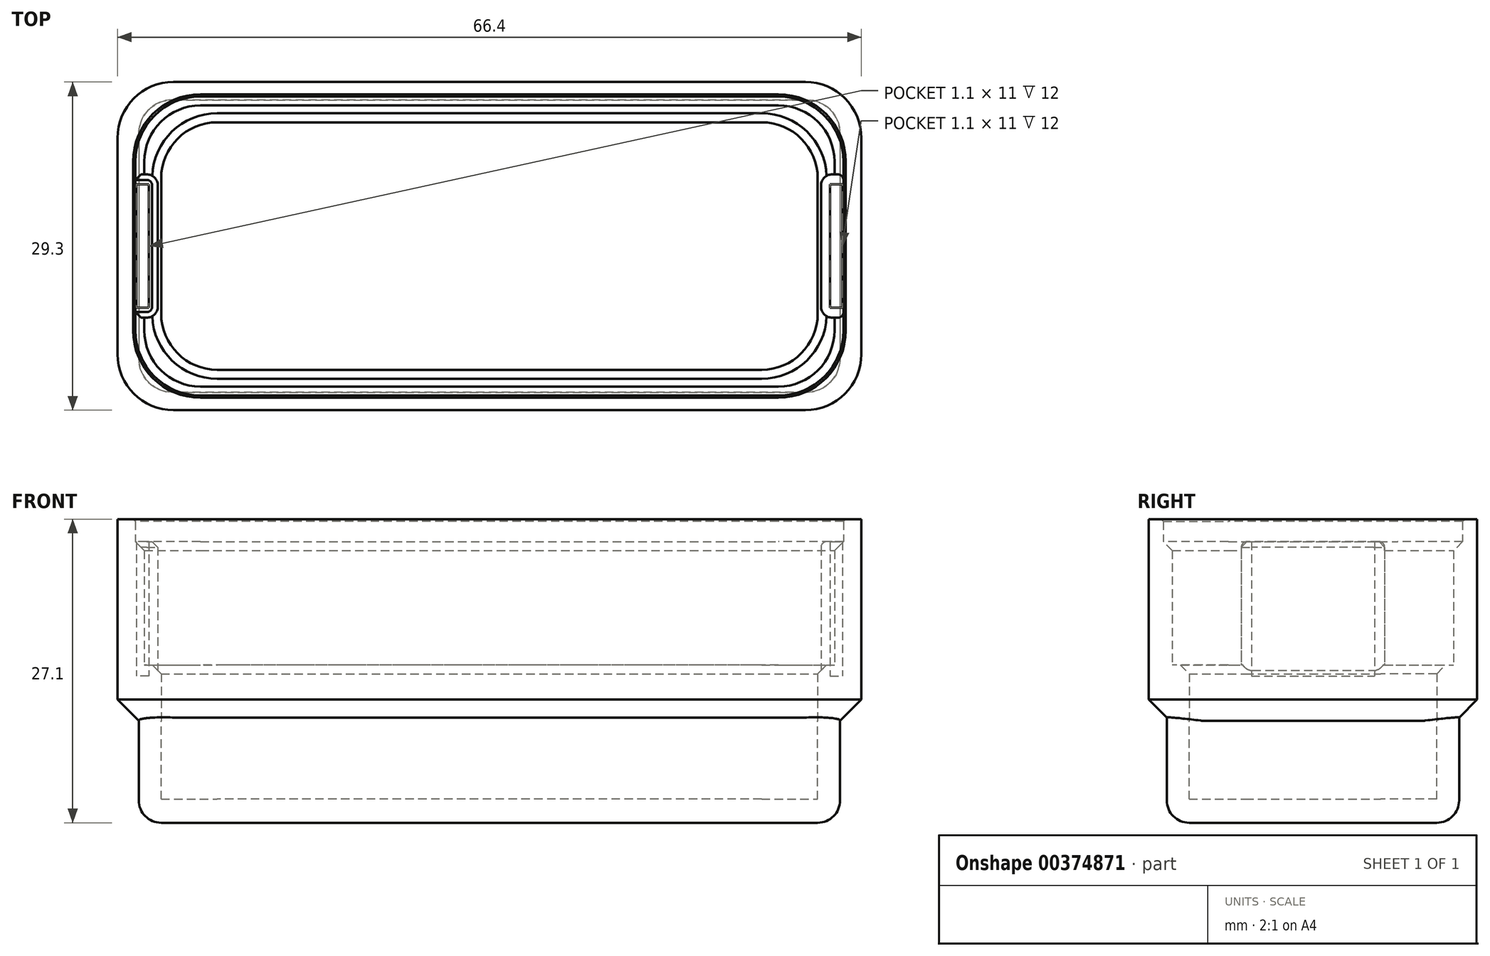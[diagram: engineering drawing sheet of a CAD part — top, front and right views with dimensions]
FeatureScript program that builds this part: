
annotation { "Feature Type Name" : "Feature", "Feature Type Description" : "" }
export const myFeature = defineFeature(function(context is Context, id is Id, definition is map)
    precondition{}
    {
        {
            var Q0;
            Q0=qCreatedBy(makeId("Top.planeOp"),FACE);
            var sketch = newSketch(context, id + "F0", { "sketchPlane" : qUnion([Q0])});
            skLineSegment(sketch, "E0.bottom", {"start": v(30.5, -12.25) * mm, "end": v(-30.5, -12.25) * mm, "construction": true});
            skLineSegment(sketch, "E0.top", {"start": v(30.5, 12.25) * mm, "end": v(-30.5, 12.25) * mm, "construction": true});
            skLineSegment(sketch, "E0.left", {"start": v(30.5, -12.25) * mm, "end": v(30.5, 12.25) * mm, "construction": true});
            skLineSegment(sketch, "E0.right", {"start": v(-30.5, -12.25) * mm, "end": v(-30.5, 12.25) * mm, "construction": true});
            skPoint(sketch, "E0.middle", {"position": v(0, 0) * mm});
            skLineSegment(sketch, "E1.bottom", {"start": v(30.8, -12.55) * mm, "end": v(-30.8, -12.55) * mm});
            skLineSegment(sketch, "E1.top", {"start": v(30.8, 12.55) * mm, "end": v(-30.8, 12.55) * mm});
            skLineSegment(sketch, "E1.left", {"start": v(30.8, -12.55) * mm, "end": v(30.8, 12.55) * mm});
            skLineSegment(sketch, "E1.right", {"start": v(-30.8, -12.55) * mm, "end": v(-30.8, -6.4) * mm});
            skLineSegment(sketch, "E2.bottom", {"start": v(33.2, -14.65) * mm, "end": v(-33.2, -14.65) * mm});
            skLineSegment(sketch, "E2.top", {"start": v(33.2, 14.65) * mm, "end": v(-33.2, 14.65) * mm});
            skLineSegment(sketch, "E2.left", {"start": v(33.2, -14.65) * mm, "end": v(33.2, 14.65) * mm});
            skLineSegment(sketch, "E2.right", {"start": v(-33.2, -14.65) * mm, "end": v(-33.2, 14.65) * mm});
            skPoint(sketch, "E3.middle", {"position": v(0, 14.35) * mm});
            skPoint(sketch, "E4.middle", {"position": v(0, -14.35) * mm});
            skPoint(sketch, "E4.middle.positionSnap0", {"position": v(0, -12.25) * mm});
            skPoint(sketch, "E4.centerSnap0", {"position": v(0, -12.25) * mm});
            skLineSegment(sketch, "E5.bottom", {"start": v(-29.6, -6.4) * mm, "end": v(-30.8, -6.4) * mm});
            skLineSegment(sketch, "E5.top", {"start": v(-29.6, 6.4) * mm, "end": v(-30.8, 6.4) * mm});
            skLineSegment(sketch, "E5.left", {"start": v(-29.6, -6.4) * mm, "end": v(-29.6, 6.4) * mm});
            skLineSegment(sketch, "E6.trimOffspring", {"start": v(-30.8, 6.4) * mm, "end": v(-30.8, 12.55) * mm});
            skLineSegment(sketch, "E7.bottom", {"start": v(-30.4, -5.5) * mm, "end": v(-31.5, -5.5) * mm});
            skLineSegment(sketch, "E7.top", {"start": v(-30.4, 5.5) * mm, "end": v(-31.5, 5.5) * mm});
            skLineSegment(sketch, "E7.left", {"start": v(-30.4, -5.5) * mm, "end": v(-30.4, 5.5) * mm});
            skLineSegment(sketch, "E7.right", {"start": v(-31.5, -5.5) * mm, "end": v(-31.5, 5.5) * mm});
            skPoint(sketch, "E8", {"position": v(-29.6, 0) * mm});
            skPoint(sketch, "E9", {"position": v(-30.4, 0) * mm});
            skLineSegment(sketch, "E10", {"start": v(0, 20.82) * mm, "end": v(0, -18.98) * mm, "construction": true});
            skLineSegment(sketch, "E11.MirrorCS", {"start": v(30.4, 5.5) * mm, "end": v(31.5, 5.5) * mm});
            skLineSegment(sketch, "E12.MirrorCS", {"start": v(30.4, -5.5) * mm, "end": v(30.4, 5.5) * mm});
            skLineSegment(sketch, "E13.MirrorCS", {"start": v(31.5, -5.5) * mm, "end": v(31.5, 5.5) * mm});
            skLineSegment(sketch, "E14.MirrorCS", {"start": v(30.4, -5.5) * mm, "end": v(31.5, -5.5) * mm});
            skLineSegment(sketch, "E15.MirrorCS", {"start": v(29.6, -6.4) * mm, "end": v(29.6, 6.4) * mm});
            skLineSegment(sketch, "E16.MirrorCS", {"start": v(29.6, -6.4) * mm, "end": v(30.8, -6.4) * mm});
            skLineSegment(sketch, "E17.MirrorCS", {"start": v(29.6, 6.4) * mm, "end": v(30.8, 6.4) * mm});
            skSolve(sketch);
        }
        {
            var Q0;
            Q0=makeQuery(id+"F0.imprint","IMPRINT",FACE,{"disambiguationData":[TD([[makeQuery(id+"F0.imprint","IMPRINT",EDGE,{"derivedFrom":sQuery(id+"F0.wireOp",EDGE,"E4.bottom")}),-1.0]])]});
            var Q1;
            Q1=makeQuery(id+"F0.imprint","IMPRINT",FACE,{"disambiguationData":[TD([[makeQuery(id+"F0.imprint","IMPRINT",EDGE,{"derivedFrom":sQuery(id+"F0.wireOp",EDGE,"E3.bottom")}),-1.0]])]});
            var Q2;
            {var subQ0=sQuery(id+"F0.wireOp",EDGE,"E12.MirrorCS");Q2=makeQuery(id+"F0.imprint","IMPRINT",FACE,{"disambiguationData":[TD([[makeQuery(id+"F0.imprint","IMPRINT",EDGE,{"derivedFrom":subQ0}),1.0]])]});}
            var Q3;
            Q3=makeQuery(id+"F0.imprint","IMPRINT",FACE,{"disambiguationData":[TD([[makeQuery(id+"F0.imprint","IMPRINT",EDGE,{"derivedFrom":sQuery(id+"F0.wireOp",EDGE,"E7.bottom")}),-1.0]])]});
            var Q4;
            {var subQ5=sQuery(id+"F0.wireOp",EDGE,"E1.bottom");Q4=makeQuery(id+"F0.imprint","IMPRINT",FACE,{"disambiguationData":[TD([[makeQuery(id+"F0.imprint","IMPRINT",EDGE,{"derivedFrom":subQ5}),1.0]])]});}
            var Q5;
            {var subQ5=sQuery(id+"F0.wireOp",EDGE,"E13.MirrorCS");Q5=makeQuery(id+"F0.imprint","IMPRINT",FACE,{"disambiguationData":[TD([[makeQuery(id+"F0.imprint","IMPRINT",EDGE,{"derivedFrom":subQ5}),1.0]])]});}
            var Q6;
            {var subQ0=sQuery(id+"F0.wireOp",EDGE,"E1.bottom");Q6=makeQuery(id+"F0.imprint","IMPRINT",FACE,{"disambiguationData":[TD([[makeQuery(id+"F0.imprint","IMPRINT",EDGE,{"derivedFrom":subQ0}),-1.0]])]});}
            var Q7;
            {var subQ5=sQuery(id+"F0.wireOp",EDGE,"E12.MirrorCS");Q7=makeQuery(id+"F0.imprint","IMPRINT",FACE,{"disambiguationData":[TD([[makeQuery(id+"F0.imprint","IMPRINT",EDGE,{"derivedFrom":subQ5}),-1.0]])]});}
            extrude(context, id + "F1", {"entities" : qUnion([Q0, Q1, Q2, Q3, Q4, Q5, Q6, Q7]), "oppositeDirection" : true, "depth" : 0.1 * mm});
        }
        {
            var Q0;
            Q0=makeQuery(id+"F0.imprint","IMPRINT",FACE,{"disambiguationData":[TD([[makeQuery(id+"F0.imprint","IMPRINT",EDGE,{"derivedFrom":sQuery(id+"F0.wireOp",EDGE,"E1.bottom")}),1.0]])]});
            var Q1;
            {var subQ0=sQuery(id+"F0.wireOp",EDGE,"E12.MirrorCS");Q1=makeQuery(id+"F0.imprint","IMPRINT",FACE,{"disambiguationData":[TD([[makeQuery(id+"F0.imprint","IMPRINT",EDGE,{"derivedFrom":subQ0}),1.0]])]});}
            extrude(context, id + "F2", {"entities" : qUnion([Q0, Q1]), "operationType" : NewBodyOperationType.ADD, "depth" : 16 * mm});
        }
        {
            var Q0;
            Q0=makeQuery(id+"F0.imprint","IMPRINT",FACE,{"disambiguationData":[TD([[makeQuery(id+"F0.imprint","IMPRINT",EDGE,{"derivedFrom":sQuery(id+"F0.wireOp",EDGE,"E1.bottom")}),-1.0]])]});
            var sketch = newSketch(context, id + "F3", { "sketchPlane" : qUnion([Q0])});
            skLineSegment(sketch, "E18.bottom", {"start": v(29.3, -11.05) * mm, "end": v(-29.3, -11.05) * mm});
            skLineSegment(sketch, "E18.top", {"start": v(29.3, 11.05) * mm, "end": v(-29.3, 11.05) * mm});
            skLineSegment(sketch, "E18.left", {"start": v(29.3, -11.05) * mm, "end": v(29.3, 11.05) * mm});
            skLineSegment(sketch, "E18.right", {"start": v(-29.3, -11.05) * mm, "end": v(-29.3, 11.05) * mm});
            skPoint(sketch, "E18.middle", {"position": v(0, 0) * mm});
            skSolve(sketch);
        }
        {
            var Q0;
            Q0 = qSketchRegion(id + "F3", true);
            extrude(context, id + "F4", {"entities" : qUnion([Q0]), "operationType" : NewBodyOperationType.REMOVE, "depth" : 25 * mm});
        }
        {
            var Q0;
            Q0=makeQuery(id+"F3.imprint","IMPRINT",FACE,{"disambiguationData":[TD([[makeQuery(id+"F3.imprint","IMPRINT",EDGE,{"derivedFrom":sQuery(id+"F3.wireOp",EDGE,"E18.bottom")}),1.0]])]});
            extrude(context, id + "F5", {"entities" : qUnion([Q0]), "operationType" : NewBodyOperationType.ADD, "depth" : 5 * mm});
        }
        {
            var Q0;
            Q0=makeQuery(id+"F0.imprint","IMPRINT",FACE,{"disambiguationData":[TD([[makeQuery(id+"F0.imprint","IMPRINT",EDGE,{"derivedFrom":sQuery(id+"F0.wireOp",EDGE,"E7.bottom")}),-1.0]])]});
            var Q1;
            {var subQ5=sQuery(id+"F0.wireOp",EDGE,"E12.MirrorCS");Q1=makeQuery(id+"F0.imprint","IMPRINT",FACE,{"disambiguationData":[TD([[makeQuery(id+"F0.imprint","IMPRINT",EDGE,{"derivedFrom":subQ5}),-1.0]])]});}
            var Q2;
            {var subQ5=sQuery(id+"F0.wireOp",EDGE,"E13.MirrorCS");Q2=makeQuery(id+"F0.imprint","IMPRINT",FACE,{"disambiguationData":[TD([[makeQuery(id+"F0.imprint","IMPRINT",EDGE,{"derivedFrom":subQ5}),1.0]])]});}
            extrude(context, id + "F6", {"entities" : qUnion([Q0, Q1, Q2]), "operationType" : NewBodyOperationType.ADD, "depth" : 4 * mm});
        }
        {
            var Q0;
            {var subQ0=sQuery(id+"F0.wireOp",EDGE,"E2.right");var subQ1=sQuery(id+"F0.wireOp",EDGE,"E2.bottom");Q0=makeQuery(id+"F2.boolean.opBoolean","MERGE",EDGE,{"derivedFrom":[makeQuery(id+"F1.opExtrude","SWEPT_EDGE",EDGE,{"disambiguationData":[OSD([subQ1,subQ0])]}),makeQuery(id+"F2.opExtrude","SWEPT_EDGE",EDGE,{"disambiguationData":[OSD([subQ1,subQ0])]})]});}
            var Q1;
            {var subQ0=sQuery(id+"F0.wireOp",EDGE,"E2.left");var subQ1=sQuery(id+"F0.wireOp",EDGE,"E2.bottom");Q1=makeQuery(id+"F2.boolean.opBoolean","MERGE",EDGE,{"derivedFrom":[makeQuery(id+"F1.opExtrude","SWEPT_EDGE",EDGE,{"disambiguationData":[OSD([subQ1,subQ0])]}),makeQuery(id+"F2.opExtrude","SWEPT_EDGE",EDGE,{"disambiguationData":[OSD([subQ1,subQ0])]})]});}
            var Q2;
            {var subQ0=sQuery(id+"F0.wireOp",EDGE,"E2.left");var subQ1=sQuery(id+"F0.wireOp",EDGE,"E2.top");Q2=makeQuery(id+"F2.boolean.opBoolean","MERGE",EDGE,{"derivedFrom":[makeQuery(id+"F1.opExtrude","SWEPT_EDGE",EDGE,{"disambiguationData":[OSD([subQ1,subQ0])]}),makeQuery(id+"F2.opExtrude","SWEPT_EDGE",EDGE,{"disambiguationData":[OSD([subQ1,subQ0])]})]});}
            var Q3;
            {var subQ0=sQuery(id+"F0.wireOp",EDGE,"E2.right");var subQ1=sQuery(id+"F0.wireOp",EDGE,"E2.top");Q3=makeQuery(id+"F2.boolean.opBoolean","MERGE",EDGE,{"derivedFrom":[makeQuery(id+"F1.opExtrude","SWEPT_EDGE",EDGE,{"disambiguationData":[OSD([subQ1,subQ0])]}),makeQuery(id+"F2.opExtrude","SWEPT_EDGE",EDGE,{"disambiguationData":[OSD([subQ1,subQ0])]})]});}
            var Q4;
            Q4=makeQuery(id+"F2.opExtrude","SWEPT_EDGE",EDGE,{"disambiguationData":[OSD([sQuery(id+"F0.wireOp",EDGE,"E1.top"),sQuery(id+"F0.wireOp",EDGE,"E6.trimOffspring")])]});
            var Q5;
            Q5=makeQuery(id+"F2.opExtrude","SWEPT_EDGE",EDGE,{"disambiguationData":[OSD([sQuery(id+"F0.wireOp",EDGE,"E1.top"),sQuery(id+"F0.wireOp",EDGE,"E1.left")])]});
            var Q6;
            Q6=makeQuery(id+"F2.opExtrude","SWEPT_EDGE",EDGE,{"disambiguationData":[OSD([sQuery(id+"F0.wireOp",EDGE,"E1.bottom"),sQuery(id+"F0.wireOp",EDGE,"E1.right")])]});
            var Q7;
            Q7=makeQuery(id+"F2.opExtrude","SWEPT_EDGE",EDGE,{"disambiguationData":[OSD([sQuery(id+"F0.wireOp",EDGE,"E1.bottom"),sQuery(id+"F0.wireOp",EDGE,"E1.left")])]});
            fillet(context, id + "F7", {"entities" : qUnion([Q0, Q1, Q2, Q3, Q4, Q5, Q6, Q7]), "radius" : 5 * mm, "tangentPropagation" : true, "allowEdgeOverflow" : false});
        }
        {
            var Q0;
            Q0=makeQuery(id+"F2.opExtrude","SWEPT_EDGE",EDGE,{"disambiguationData":[OSD([sQuery(id+"F0.wireOp",EDGE,"E5.top"),sQuery(id+"F0.wireOp",EDGE,"E5.left")])]});
            var Q1;
            Q1=makeQuery(id+"F2.opExtrude","SWEPT_EDGE",EDGE,{"disambiguationData":[OSD([sQuery(id+"F0.wireOp",EDGE,"E5.bottom"),sQuery(id+"F0.wireOp",EDGE,"E5.left")])]});
            var Q2;
            Q2=makeQuery(id+"F2.opExtrude","SWEPT_EDGE",EDGE,{"disambiguationData":[OSD([sQuery(id+"F0.wireOp",EDGE,"E15.MirrorCS"),sQuery(id+"F0.wireOp",EDGE,"E17.MirrorCS")])]});
            var Q3;
            Q3=makeQuery(id+"F2.opExtrude","SWEPT_EDGE",EDGE,{"disambiguationData":[OSD([sQuery(id+"F0.wireOp",EDGE,"E15.MirrorCS"),sQuery(id+"F0.wireOp",EDGE,"E16.MirrorCS")])]});
            fillet(context, id + "F8", {"entities" : qUnion([Q0, Q1, Q2, Q3]), "radius" : 1 * mm, "tangentPropagation" : true, "allowEdgeOverflow" : false});
        }
        {
            var Q0;
            Q0=makeQuery(id+"F5.opExtrude","SWEPT_EDGE",EDGE,{"disambiguationData":[OSD([sQuery(id+"F3.wireOp",EDGE,"E18.top"),sQuery(id+"F3.wireOp",EDGE,"E18.left")])]});
            var Q1;
            Q1=makeQuery(id+"F5.opExtrude","SWEPT_EDGE",EDGE,{"disambiguationData":[OSD([sQuery(id+"F3.wireOp",EDGE,"E18.top"),sQuery(id+"F3.wireOp",EDGE,"E18.right")])]});
            var Q2;
            Q2=makeQuery(id+"F5.opExtrude","SWEPT_EDGE",EDGE,{"disambiguationData":[OSD([sQuery(id+"F3.wireOp",EDGE,"E18.bottom"),sQuery(id+"F3.wireOp",EDGE,"E18.right")])]});
            var Q3;
            Q3=makeQuery(id+"F5.opExtrude","SWEPT_EDGE",EDGE,{"disambiguationData":[OSD([sQuery(id+"F3.wireOp",EDGE,"E18.bottom"),sQuery(id+"F3.wireOp",EDGE,"E18.left")])]});
            fillet(context, id + "F9", {"entities" : qUnion([Q0, Q1, Q2, Q3]), "radius" : 5 * mm, "tangentPropagation" : true, "allowEdgeOverflow" : false});
        }
        {
            var Q0;
            Q0=makeQuery(id+"F1.opExtrude","CAP_FACE",FACE,{"disambiguationData":[OSD([sQuery(id+"F0.wireOp",EDGE,"E2.bottom"),sQuery(id+"F0.wireOp",EDGE,"E2.top"),sQuery(id+"F0.wireOp",EDGE,"E2.left"),sQuery(id+"F0.wireOp",EDGE,"E2.right")])],"isStart":false});
            var sketch = newSketch(context, id + "F10", { "sketchPlane" : qUnion([Q0])});
            skLineSegment(sketch, "E19.bottom", {"start": v(31.3, -13.05) * mm, "end": v(-31.3, -13.05) * mm});
            skLineSegment(sketch, "E19.top", {"start": v(31.3, 13.05) * mm, "end": v(-31.3, 13.05) * mm});
            skLineSegment(sketch, "E19.left", {"start": v(31.3, -13.05) * mm, "end": v(31.3, 13.05) * mm});
            skLineSegment(sketch, "E19.right", {"start": v(-31.3, -13.05) * mm, "end": v(-31.3, 13.05) * mm});
            skPoint(sketch, "E19.middle", {"position": v(0, 0) * mm});
            skSolve(sketch);
        }
        {
            var Q0;
            Q0=makeQuery(id+"F10.imprint","IMPRINT",FACE,{"disambiguationData":[TD([[makeQuery(id+"F10.imprint","IMPRINT",EDGE,{"derivedFrom":sQuery(id+"F10.wireOp",EDGE,"E19.bottom")}),-1.0]])]});
            extrude(context, id + "F11", {"entities" : qUnion([Q0]), "operationType" : NewBodyOperationType.ADD, "depth" : 9 * mm});
        }
        {
            var Q0;
            Q0=makeQuery(id+"F3.imprint","IMPRINT",FACE,{"disambiguationData":[TD([[makeQuery(id+"F3.imprint","IMPRINT",EDGE,{"derivedFrom":sQuery(id+"F3.wireOp",EDGE,"E18.bottom")}),-1.0]])]});
            extrude(context, id + "F12", {"entities" : qUnion([Q0]), "operationType" : NewBodyOperationType.REMOVE, "oppositeDirection" : true, "depth" : 7 * mm});
        }
        {
            var Q0;
            Q0=makeQuery(id+"F12.boolean.opBoolean","COPY",EDGE,{"derivedFrom":makeQuery(id+"F12.opExtrude","SWEPT_EDGE",EDGE,{"disambiguationData":[OSD([sQuery(id+"F3.wireOp",EDGE,"E18.top"),sQuery(id+"F3.wireOp",EDGE,"E18.right")])]})});
            var Q1;
            Q1=makeQuery(id+"F12.boolean.opBoolean","COPY",EDGE,{"derivedFrom":makeQuery(id+"F12.opExtrude","SWEPT_EDGE",EDGE,{"disambiguationData":[OSD([sQuery(id+"F3.wireOp",EDGE,"E18.top"),sQuery(id+"F3.wireOp",EDGE,"E18.left")])]})});
            var Q2;
            Q2=makeQuery(id+"F12.boolean.opBoolean","COPY",EDGE,{"derivedFrom":makeQuery(id+"F12.opExtrude","SWEPT_EDGE",EDGE,{"disambiguationData":[OSD([sQuery(id+"F3.wireOp",EDGE,"E18.bottom"),sQuery(id+"F3.wireOp",EDGE,"E18.left")])]})});
            var Q3;
            Q3=makeQuery(id+"F12.boolean.opBoolean","COPY",EDGE,{"derivedFrom":makeQuery(id+"F12.opExtrude","SWEPT_EDGE",EDGE,{"disambiguationData":[OSD([sQuery(id+"F3.wireOp",EDGE,"E18.bottom"),sQuery(id+"F3.wireOp",EDGE,"E18.right")])]})});
            fillet(context, id + "F13", {"entities" : qUnion([Q0, Q1, Q2, Q3]), "radius" : 5 * mm, "tangentPropagation" : true, "allowEdgeOverflow" : false});
        }
        {
            var Q0;
            Q0=makeQuery(id+"F11.opExtrude","SWEPT_EDGE",EDGE,{"disambiguationData":[OSD([sQuery(id+"F10.wireOp",EDGE,"E19.bottom"),sQuery(id+"F10.wireOp",EDGE,"E19.right")])]});
            var Q1;
            Q1=makeQuery(id+"F11.opExtrude","SWEPT_EDGE",EDGE,{"disambiguationData":[OSD([sQuery(id+"F10.wireOp",EDGE,"E19.top"),sQuery(id+"F10.wireOp",EDGE,"E19.right")])]});
            var Q2;
            Q2=makeQuery(id+"F11.opExtrude","SWEPT_EDGE",EDGE,{"disambiguationData":[OSD([sQuery(id+"F10.wireOp",EDGE,"E19.bottom"),sQuery(id+"F10.wireOp",EDGE,"E19.left")])]});
            var Q3;
            Q3=makeQuery(id+"F11.opExtrude","SWEPT_EDGE",EDGE,{"disambiguationData":[OSD([sQuery(id+"F10.wireOp",EDGE,"E19.top"),sQuery(id+"F10.wireOp",EDGE,"E19.left")])]});
            fillet(context, id + "F14", {"entities" : qUnion([Q0, Q1, Q2, Q3]), "radius" : 3 * mm, "tangentPropagation" : true, "allowEdgeOverflow" : false});
        }
        {
            var Q0;
            Q0=makeQuery(id+"F11.opExtrude","CAP_EDGE",EDGE,{"disambiguationData":[OSD([sQuery(id+"F10.wireOp",EDGE,"E19.bottom")])],"isStart":false});
            fillet(context, id + "F15", {"entities" : qUnion([Q0]), "radius" : 2 * mm, "tangentPropagation" : true, "allowEdgeOverflow" : false});
        }
        {
            var Q0;
            Q0=makeQuery(id+"F1.opExtrude","CAP_EDGE",EDGE,{"disambiguationData":[OSD([sQuery(id+"F0.wireOp",EDGE,"E2.top")])],"isStart":false});
            chamfer(context, id + "F16", {"entities" : qUnion([Q0]), "width" : 2 * mm, "tangentPropagation" : true});
        }
        {
            var Q0;
            Q0=makeQuery(id+"F2.opExtrude","CAP_EDGE",EDGE,{"disambiguationData":[OSD([sQuery(id+"F0.wireOp",EDGE,"E1.bottom")])],"isStart":false});
            var Q1;
            Q1=makeQuery(id+"F2.opExtrude","CAP_EDGE",EDGE,{"disambiguationData":[OSD([sQuery(id+"F0.wireOp",EDGE,"E1.top")])],"isStart":false});
            var Q2;
            Q2=makeQuery(id+"F5.opExtrude","CAP_EDGE",EDGE,{"disambiguationData":[OSD([sQuery(id+"F3.wireOp",EDGE,"E18.top")])],"isStart":false});
            chamfer(context, id + "F17", {"entities" : qUnion([Q0, Q1, Q2]), "width" : 0.8 * mm, "tangentPropagation" : true});
        }
        {
            var Q0;
            Q0=makeQuery(id+"F2.opExtrude","CAP_EDGE",EDGE,{"disambiguationData":[OSD([sQuery(id+"F0.wireOp",EDGE,"E5.left")])],"isStart":false});
            chamfer(context, id + "F18", {"entities" : qUnion([Q0]), "width" : 0.5 * mm, "tangentPropagation" : true});
        }
        {
            var Q0;
            Q0=makeQuery(id+"F2.opExtrude","CAP_EDGE",EDGE,{"disambiguationData":[OSD([sQuery(id+"F0.wireOp",EDGE,"E15.MirrorCS")])],"isStart":false});
            fillet(context, id + "F19", {"entities" : qUnion([Q0]), "radius" : 0.5 * mm, "tangentPropagation" : true, "allowEdgeOverflow" : false});
        }
        {
            var Q0;
            Q0=makeQuery(id+"F2.opExtrude","CAP_FACE",FACE,{"disambiguationData":[OSD([sQuery(id+"F0.wireOp",EDGE,"E1.bottom"),sQuery(id+"F0.wireOp",EDGE,"E1.top"),sQuery(id+"F0.wireOp",EDGE,"E1.left"),sQuery(id+"F0.wireOp",EDGE,"E1.right"),sQuery(id+"F0.wireOp",EDGE,"E2.bottom"),sQuery(id+"F0.wireOp",EDGE,"E2.top"),sQuery(id+"F0.wireOp",EDGE,"E2.left"),sQuery(id+"F0.wireOp",EDGE,"E2.right"),sQuery(id+"F0.wireOp",EDGE,"E5.bottom"),sQuery(id+"F0.wireOp",EDGE,"E5.top"),sQuery(id+"F0.wireOp",EDGE,"E5.left"),sQuery(id+"F0.wireOp",EDGE,"E6.trimOffspring"),sQuery(id+"F0.wireOp",EDGE,"E7.bottom"),sQuery(id+"F0.wireOp",EDGE,"E7.top"),sQuery(id+"F0.wireOp",EDGE,"E7.left"),sQuery(id+"F0.wireOp",EDGE,"E7.right"),sQuery(id+"F0.wireOp",EDGE,"E11.MirrorCS"),sQuery(id+"F0.wireOp",EDGE,"E12.MirrorCS"),sQuery(id+"F0.wireOp",EDGE,"E13.MirrorCS"),sQuery(id+"F0.wireOp",EDGE,"E14.MirrorCS"),sQuery(id+"F0.wireOp",EDGE,"E15.MirrorCS"),sQuery(id+"F0.wireOp",EDGE,"E16.MirrorCS"),sQuery(id+"F0.wireOp",EDGE,"E17.MirrorCS")])],"isStart":false});
            var sketch = newSketch(context, id + "F20", { "sketchPlane" : qUnion([Q0])});
            skLineSegment(sketch, "E20", {"start": v(-31.6, 5.9) * mm, "end": v(-31.6, -5.9) * mm});
            skLineSegment(sketch, "E21", {"start": v(31.6, 5.9) * mm, "end": v(31.6, -5.9) * mm});
            skSolve(sketch);
        }
        {
            var Q0;
            Q0=makeQuery(id+"F20.imprint","IMPRINT",FACE,{"disambiguationData":[TD([[makeQuery(id+"F20.imprint","IMPRINT",EDGE,{"derivedFrom":sQuery(id+"F20.wireOp",EDGE,"E20")}),-1.0]])]});
            extrude(context, id + "F21", {"entities" : qUnion([Q0]), "operationType" : NewBodyOperationType.ADD, "depth" : 2 * mm});
        }
        {
            var Q0;
            {var subQ0=sQuery(id+"F0.wireOp",EDGE,"E17.MirrorCS");var subQ1=sQuery(id+"F0.wireOp",EDGE,"E16.MirrorCS");var subQ2=sQuery(id+"F0.wireOp",EDGE,"E15.MirrorCS");var subQ3=sQuery(id+"F0.wireOp",EDGE,"E14.MirrorCS");var subQ4=sQuery(id+"F0.wireOp",EDGE,"E13.MirrorCS");var subQ5=sQuery(id+"F0.wireOp",EDGE,"E12.MirrorCS");var subQ6=sQuery(id+"F0.wireOp",EDGE,"E11.MirrorCS");var subQ7=sQuery(id+"F0.wireOp",EDGE,"E7.right");var subQ8=sQuery(id+"F0.wireOp",EDGE,"E7.left");var subQ9=sQuery(id+"F0.wireOp",EDGE,"E7.top");var subQ10=sQuery(id+"F0.wireOp",EDGE,"E7.bottom");var subQ11=sQuery(id+"F0.wireOp",EDGE,"E6.trimOffspring");var subQ12=sQuery(id+"F0.wireOp",EDGE,"E5.left");var subQ13=sQuery(id+"F0.wireOp",EDGE,"E5.top");var subQ14=sQuery(id+"F0.wireOp",EDGE,"E5.bottom");var subQ15=sQuery(id+"F0.wireOp",EDGE,"E2.right");var subQ16=sQuery(id+"F0.wireOp",EDGE,"E2.left");var subQ17=sQuery(id+"F0.wireOp",EDGE,"E2.top");var subQ18=sQuery(id+"F0.wireOp",EDGE,"E2.bottom");var subQ19=sQuery(id+"F0.wireOp",EDGE,"E1.right");var subQ20=sQuery(id+"F0.wireOp",EDGE,"E1.left");var subQ21=sQuery(id+"F0.wireOp",EDGE,"E1.top");var subQ22=sQuery(id+"F0.wireOp",EDGE,"E1.bottom");Q0=makeQuery(id+"F21.opExtrude","CAP_EDGE",EDGE,{"disambiguationData":[OSD([subQ22,subQ21,subQ20,subQ19,subQ18,subQ17,subQ16,subQ15,subQ14,subQ13,subQ12,subQ11,subQ10,subQ9,subQ8,subQ7,subQ6,subQ5,subQ4,subQ3,subQ2,subQ1,subQ0]),TDD([makeQuery(id+"F20.imprint","IMPRINT",EDGE,{"derivedFrom":makeQuery(id+"F17.opChamfer","BLEND_EDGE",EDGE,{"blendedFrom":[makeQuery(id+"F2.opExtrude","CAP_EDGE",EDGE,{"disambiguationData":[OSD([subQ21])],"isStart":false}),makeQuery(id+"F2.opExtrude","CAP_FACE",FACE,{"disambiguationData":[OSD([subQ22,subQ21,subQ20,subQ19,subQ18,subQ17,subQ16,subQ15,subQ14,subQ13,subQ12,subQ11,subQ10,subQ9,subQ8,subQ7,subQ6,subQ5,subQ4,subQ3,subQ2,subQ1,subQ0])],"isStart":false})],"blendedInto":[makeQuery(id+"F2.opExtrude","CAP_FACE",FACE,{"disambiguationData":[OSD([subQ22,subQ21,subQ20,subQ19,subQ18,subQ17,subQ16,subQ15,subQ14,subQ13,subQ12,subQ11,subQ10,subQ9,subQ8,subQ7,subQ6,subQ5,subQ4,subQ3,subQ2,subQ1,subQ0])],"isStart":false})]})})])],"isStart":false});}
            var Q1;
            {var subQ0=sQuery(id+"F0.wireOp",EDGE,"E17.MirrorCS");var subQ1=sQuery(id+"F0.wireOp",EDGE,"E16.MirrorCS");var subQ2=sQuery(id+"F0.wireOp",EDGE,"E15.MirrorCS");var subQ3=sQuery(id+"F0.wireOp",EDGE,"E14.MirrorCS");var subQ4=sQuery(id+"F0.wireOp",EDGE,"E13.MirrorCS");var subQ5=sQuery(id+"F0.wireOp",EDGE,"E12.MirrorCS");var subQ6=sQuery(id+"F0.wireOp",EDGE,"E11.MirrorCS");var subQ7=sQuery(id+"F0.wireOp",EDGE,"E7.right");var subQ8=sQuery(id+"F0.wireOp",EDGE,"E7.left");var subQ9=sQuery(id+"F0.wireOp",EDGE,"E7.top");var subQ10=sQuery(id+"F0.wireOp",EDGE,"E7.bottom");var subQ11=sQuery(id+"F0.wireOp",EDGE,"E6.trimOffspring");var subQ12=sQuery(id+"F0.wireOp",EDGE,"E5.left");var subQ13=sQuery(id+"F0.wireOp",EDGE,"E5.top");var subQ14=sQuery(id+"F0.wireOp",EDGE,"E5.bottom");var subQ15=sQuery(id+"F0.wireOp",EDGE,"E2.right");var subQ16=sQuery(id+"F0.wireOp",EDGE,"E2.left");var subQ17=sQuery(id+"F0.wireOp",EDGE,"E2.top");var subQ18=sQuery(id+"F0.wireOp",EDGE,"E2.bottom");var subQ19=sQuery(id+"F0.wireOp",EDGE,"E1.right");var subQ20=sQuery(id+"F0.wireOp",EDGE,"E1.left");var subQ21=sQuery(id+"F0.wireOp",EDGE,"E1.top");var subQ22=sQuery(id+"F0.wireOp",EDGE,"E1.bottom");var subQ23=makeQuery(id+"F2.opExtrude","CAP_FACE",FACE,{"disambiguationData":[OSD([subQ22,subQ21,subQ20,subQ19,subQ18,subQ17,subQ16,subQ15,subQ14,subQ13,subQ12,subQ11,subQ10,subQ9,subQ8,subQ7,subQ6,subQ5,subQ4,subQ3,subQ2,subQ1,subQ0])],"isStart":false});Q1=makeQuery(id+"F21.opExtrude","CAP_EDGE",EDGE,{"disambiguationData":[OSD([subQ22,subQ21,subQ20,subQ19,subQ18,subQ17,subQ16,subQ15,subQ14,subQ13,subQ12,subQ11,subQ10,subQ9,subQ8,subQ7,subQ6,subQ5,subQ4,subQ3,subQ2,subQ1,subQ0]),TDD([makeQuery(id+"F20.imprint","IMPRINT",EDGE,{"derivedFrom":makeQuery(id+"F17.opChamfer","BLEND_EDGE",EDGE,{"blendedFrom":[makeQuery(id+"F7.opFillet","BLEND_EDGE",EDGE,{"blendedFrom":[makeQuery(id+"F2.opExtrude","SWEPT_EDGE",EDGE,{"disambiguationData":[OSD([subQ21,subQ11])]}),subQ23],"blendedInto":[subQ23]}),subQ23],"blendedInto":[subQ23]})})])],"isStart":false});}
            var Q2;
            Q2=makeQuery(id+"F21.opExtrude","CAP_EDGE",EDGE,{"disambiguationData":[OSD([sQuery(id+"F0.wireOp",EDGE,"E1.bottom"),sQuery(id+"F0.wireOp",EDGE,"E1.top"),sQuery(id+"F0.wireOp",EDGE,"E1.left"),sQuery(id+"F0.wireOp",EDGE,"E1.right"),sQuery(id+"F0.wireOp",EDGE,"E2.bottom"),sQuery(id+"F0.wireOp",EDGE,"E2.top"),sQuery(id+"F0.wireOp",EDGE,"E2.left"),sQuery(id+"F0.wireOp",EDGE,"E2.right"),sQuery(id+"F0.wireOp",EDGE,"E5.bottom"),sQuery(id+"F0.wireOp",EDGE,"E5.top"),sQuery(id+"F0.wireOp",EDGE,"E5.left"),sQuery(id+"F0.wireOp",EDGE,"E6.trimOffspring"),sQuery(id+"F0.wireOp",EDGE,"E7.bottom"),sQuery(id+"F0.wireOp",EDGE,"E7.top"),sQuery(id+"F0.wireOp",EDGE,"E7.left"),sQuery(id+"F0.wireOp",EDGE,"E7.right"),sQuery(id+"F0.wireOp",EDGE,"E11.MirrorCS"),sQuery(id+"F0.wireOp",EDGE,"E12.MirrorCS"),sQuery(id+"F0.wireOp",EDGE,"E13.MirrorCS"),sQuery(id+"F0.wireOp",EDGE,"E14.MirrorCS"),sQuery(id+"F0.wireOp",EDGE,"E15.MirrorCS"),sQuery(id+"F0.wireOp",EDGE,"E16.MirrorCS"),sQuery(id+"F0.wireOp",EDGE,"E17.MirrorCS"),sQuery(id+"F20.wireOp",EDGE,"E20")])],"isStart":false});
            var Q3;
            {var subQ0=sQuery(id+"F0.wireOp",EDGE,"E17.MirrorCS");var subQ1=sQuery(id+"F0.wireOp",EDGE,"E16.MirrorCS");var subQ2=sQuery(id+"F0.wireOp",EDGE,"E15.MirrorCS");var subQ3=sQuery(id+"F0.wireOp",EDGE,"E14.MirrorCS");var subQ4=sQuery(id+"F0.wireOp",EDGE,"E13.MirrorCS");var subQ5=sQuery(id+"F0.wireOp",EDGE,"E12.MirrorCS");var subQ6=sQuery(id+"F0.wireOp",EDGE,"E11.MirrorCS");var subQ7=sQuery(id+"F0.wireOp",EDGE,"E7.right");var subQ8=sQuery(id+"F0.wireOp",EDGE,"E7.left");var subQ9=sQuery(id+"F0.wireOp",EDGE,"E7.top");var subQ10=sQuery(id+"F0.wireOp",EDGE,"E7.bottom");var subQ11=sQuery(id+"F0.wireOp",EDGE,"E6.trimOffspring");var subQ12=sQuery(id+"F0.wireOp",EDGE,"E5.left");var subQ13=sQuery(id+"F0.wireOp",EDGE,"E5.top");var subQ14=sQuery(id+"F0.wireOp",EDGE,"E5.bottom");var subQ15=sQuery(id+"F0.wireOp",EDGE,"E2.right");var subQ16=sQuery(id+"F0.wireOp",EDGE,"E2.left");var subQ17=sQuery(id+"F0.wireOp",EDGE,"E2.top");var subQ18=sQuery(id+"F0.wireOp",EDGE,"E2.bottom");var subQ19=sQuery(id+"F0.wireOp",EDGE,"E1.right");var subQ20=sQuery(id+"F0.wireOp",EDGE,"E1.left");var subQ21=sQuery(id+"F0.wireOp",EDGE,"E1.top");var subQ22=sQuery(id+"F0.wireOp",EDGE,"E1.bottom");var subQ23=makeQuery(id+"F2.opExtrude","CAP_FACE",FACE,{"disambiguationData":[OSD([subQ22,subQ21,subQ20,subQ19,subQ18,subQ17,subQ16,subQ15,subQ14,subQ13,subQ12,subQ11,subQ10,subQ9,subQ8,subQ7,subQ6,subQ5,subQ4,subQ3,subQ2,subQ1,subQ0])],"isStart":false});Q3=makeQuery(id+"F21.opExtrude","CAP_EDGE",EDGE,{"disambiguationData":[OSD([subQ22,subQ21,subQ20,subQ19,subQ18,subQ17,subQ16,subQ15,subQ14,subQ13,subQ12,subQ11,subQ10,subQ9,subQ8,subQ7,subQ6,subQ5,subQ4,subQ3,subQ2,subQ1,subQ0]),TDD([makeQuery(id+"F20.imprint","IMPRINT",EDGE,{"derivedFrom":makeQuery(id+"F17.opChamfer","BLEND_EDGE",EDGE,{"blendedFrom":[makeQuery(id+"F7.opFillet","BLEND_EDGE",EDGE,{"blendedFrom":[makeQuery(id+"F2.opExtrude","SWEPT_EDGE",EDGE,{"disambiguationData":[OSD([subQ22,subQ19])]}),subQ23],"blendedInto":[subQ23]}),subQ23],"blendedInto":[subQ23]})})])],"isStart":false});}
            var Q4;
            {var subQ0=sQuery(id+"F0.wireOp",EDGE,"E17.MirrorCS");var subQ1=sQuery(id+"F0.wireOp",EDGE,"E16.MirrorCS");var subQ2=sQuery(id+"F0.wireOp",EDGE,"E15.MirrorCS");var subQ3=sQuery(id+"F0.wireOp",EDGE,"E14.MirrorCS");var subQ4=sQuery(id+"F0.wireOp",EDGE,"E13.MirrorCS");var subQ5=sQuery(id+"F0.wireOp",EDGE,"E12.MirrorCS");var subQ6=sQuery(id+"F0.wireOp",EDGE,"E11.MirrorCS");var subQ7=sQuery(id+"F0.wireOp",EDGE,"E7.right");var subQ8=sQuery(id+"F0.wireOp",EDGE,"E7.left");var subQ9=sQuery(id+"F0.wireOp",EDGE,"E7.top");var subQ10=sQuery(id+"F0.wireOp",EDGE,"E7.bottom");var subQ11=sQuery(id+"F0.wireOp",EDGE,"E6.trimOffspring");var subQ12=sQuery(id+"F0.wireOp",EDGE,"E5.left");var subQ13=sQuery(id+"F0.wireOp",EDGE,"E5.top");var subQ14=sQuery(id+"F0.wireOp",EDGE,"E5.bottom");var subQ15=sQuery(id+"F0.wireOp",EDGE,"E2.right");var subQ16=sQuery(id+"F0.wireOp",EDGE,"E2.left");var subQ17=sQuery(id+"F0.wireOp",EDGE,"E2.top");var subQ18=sQuery(id+"F0.wireOp",EDGE,"E2.bottom");var subQ19=sQuery(id+"F0.wireOp",EDGE,"E1.right");var subQ20=sQuery(id+"F0.wireOp",EDGE,"E1.left");var subQ21=sQuery(id+"F0.wireOp",EDGE,"E1.top");var subQ22=sQuery(id+"F0.wireOp",EDGE,"E1.bottom");Q4=makeQuery(id+"F21.opExtrude","CAP_EDGE",EDGE,{"disambiguationData":[OSD([subQ22,subQ21,subQ20,subQ19,subQ18,subQ17,subQ16,subQ15,subQ14,subQ13,subQ12,subQ11,subQ10,subQ9,subQ8,subQ7,subQ6,subQ5,subQ4,subQ3,subQ2,subQ1,subQ0]),TDD([makeQuery(id+"F20.imprint","IMPRINT",EDGE,{"derivedFrom":makeQuery(id+"F17.opChamfer","BLEND_EDGE",EDGE,{"blendedFrom":[makeQuery(id+"F2.opExtrude","CAP_EDGE",EDGE,{"disambiguationData":[OSD([subQ22])],"isStart":false}),makeQuery(id+"F2.opExtrude","CAP_FACE",FACE,{"disambiguationData":[OSD([subQ22,subQ21,subQ20,subQ19,subQ18,subQ17,subQ16,subQ15,subQ14,subQ13,subQ12,subQ11,subQ10,subQ9,subQ8,subQ7,subQ6,subQ5,subQ4,subQ3,subQ2,subQ1,subQ0])],"isStart":false})],"blendedInto":[makeQuery(id+"F2.opExtrude","CAP_FACE",FACE,{"disambiguationData":[OSD([subQ22,subQ21,subQ20,subQ19,subQ18,subQ17,subQ16,subQ15,subQ14,subQ13,subQ12,subQ11,subQ10,subQ9,subQ8,subQ7,subQ6,subQ5,subQ4,subQ3,subQ2,subQ1,subQ0])],"isStart":false})]})})])],"isStart":false});}
            var Q5;
            {var subQ0=sQuery(id+"F0.wireOp",EDGE,"E17.MirrorCS");var subQ1=sQuery(id+"F0.wireOp",EDGE,"E16.MirrorCS");var subQ2=sQuery(id+"F0.wireOp",EDGE,"E15.MirrorCS");var subQ3=sQuery(id+"F0.wireOp",EDGE,"E14.MirrorCS");var subQ4=sQuery(id+"F0.wireOp",EDGE,"E13.MirrorCS");var subQ5=sQuery(id+"F0.wireOp",EDGE,"E12.MirrorCS");var subQ6=sQuery(id+"F0.wireOp",EDGE,"E11.MirrorCS");var subQ7=sQuery(id+"F0.wireOp",EDGE,"E7.right");var subQ8=sQuery(id+"F0.wireOp",EDGE,"E7.left");var subQ9=sQuery(id+"F0.wireOp",EDGE,"E7.top");var subQ10=sQuery(id+"F0.wireOp",EDGE,"E7.bottom");var subQ11=sQuery(id+"F0.wireOp",EDGE,"E6.trimOffspring");var subQ12=sQuery(id+"F0.wireOp",EDGE,"E5.left");var subQ13=sQuery(id+"F0.wireOp",EDGE,"E5.top");var subQ14=sQuery(id+"F0.wireOp",EDGE,"E5.bottom");var subQ15=sQuery(id+"F0.wireOp",EDGE,"E2.right");var subQ16=sQuery(id+"F0.wireOp",EDGE,"E2.left");var subQ17=sQuery(id+"F0.wireOp",EDGE,"E2.top");var subQ18=sQuery(id+"F0.wireOp",EDGE,"E2.bottom");var subQ19=sQuery(id+"F0.wireOp",EDGE,"E1.right");var subQ20=sQuery(id+"F0.wireOp",EDGE,"E1.left");var subQ21=sQuery(id+"F0.wireOp",EDGE,"E1.top");var subQ22=sQuery(id+"F0.wireOp",EDGE,"E1.bottom");var subQ23=makeQuery(id+"F2.opExtrude","CAP_FACE",FACE,{"disambiguationData":[OSD([subQ22,subQ21,subQ20,subQ19,subQ18,subQ17,subQ16,subQ15,subQ14,subQ13,subQ12,subQ11,subQ10,subQ9,subQ8,subQ7,subQ6,subQ5,subQ4,subQ3,subQ2,subQ1,subQ0])],"isStart":false});Q5=makeQuery(id+"F21.opExtrude","CAP_EDGE",EDGE,{"disambiguationData":[OSD([subQ22,subQ21,subQ20,subQ19,subQ18,subQ17,subQ16,subQ15,subQ14,subQ13,subQ12,subQ11,subQ10,subQ9,subQ8,subQ7,subQ6,subQ5,subQ4,subQ3,subQ2,subQ1,subQ0]),TDD([makeQuery(id+"F20.imprint","IMPRINT",EDGE,{"derivedFrom":makeQuery(id+"F17.opChamfer","BLEND_EDGE",EDGE,{"blendedFrom":[makeQuery(id+"F7.opFillet","BLEND_EDGE",EDGE,{"blendedFrom":[makeQuery(id+"F2.opExtrude","SWEPT_EDGE",EDGE,{"disambiguationData":[OSD([subQ22,subQ20])]}),subQ23],"blendedInto":[subQ23]}),subQ23],"blendedInto":[subQ23]})})])],"isStart":false});}
            var Q6;
            Q6=makeQuery(id+"F21.opExtrude","CAP_EDGE",EDGE,{"disambiguationData":[OSD([sQuery(id+"F0.wireOp",EDGE,"E1.bottom"),sQuery(id+"F0.wireOp",EDGE,"E1.top"),sQuery(id+"F0.wireOp",EDGE,"E1.left"),sQuery(id+"F0.wireOp",EDGE,"E1.right"),sQuery(id+"F0.wireOp",EDGE,"E2.bottom"),sQuery(id+"F0.wireOp",EDGE,"E2.top"),sQuery(id+"F0.wireOp",EDGE,"E2.left"),sQuery(id+"F0.wireOp",EDGE,"E2.right"),sQuery(id+"F0.wireOp",EDGE,"E5.bottom"),sQuery(id+"F0.wireOp",EDGE,"E5.top"),sQuery(id+"F0.wireOp",EDGE,"E5.left"),sQuery(id+"F0.wireOp",EDGE,"E6.trimOffspring"),sQuery(id+"F0.wireOp",EDGE,"E7.bottom"),sQuery(id+"F0.wireOp",EDGE,"E7.top"),sQuery(id+"F0.wireOp",EDGE,"E7.left"),sQuery(id+"F0.wireOp",EDGE,"E7.right"),sQuery(id+"F0.wireOp",EDGE,"E11.MirrorCS"),sQuery(id+"F0.wireOp",EDGE,"E12.MirrorCS"),sQuery(id+"F0.wireOp",EDGE,"E13.MirrorCS"),sQuery(id+"F0.wireOp",EDGE,"E14.MirrorCS"),sQuery(id+"F0.wireOp",EDGE,"E15.MirrorCS"),sQuery(id+"F0.wireOp",EDGE,"E16.MirrorCS"),sQuery(id+"F0.wireOp",EDGE,"E17.MirrorCS"),sQuery(id+"F20.wireOp",EDGE,"E21")])],"isStart":false});
            var Q7;
            {var subQ0=sQuery(id+"F0.wireOp",EDGE,"E17.MirrorCS");var subQ1=sQuery(id+"F0.wireOp",EDGE,"E16.MirrorCS");var subQ2=sQuery(id+"F0.wireOp",EDGE,"E15.MirrorCS");var subQ3=sQuery(id+"F0.wireOp",EDGE,"E14.MirrorCS");var subQ4=sQuery(id+"F0.wireOp",EDGE,"E13.MirrorCS");var subQ5=sQuery(id+"F0.wireOp",EDGE,"E12.MirrorCS");var subQ6=sQuery(id+"F0.wireOp",EDGE,"E11.MirrorCS");var subQ7=sQuery(id+"F0.wireOp",EDGE,"E7.right");var subQ8=sQuery(id+"F0.wireOp",EDGE,"E7.left");var subQ9=sQuery(id+"F0.wireOp",EDGE,"E7.top");var subQ10=sQuery(id+"F0.wireOp",EDGE,"E7.bottom");var subQ11=sQuery(id+"F0.wireOp",EDGE,"E6.trimOffspring");var subQ12=sQuery(id+"F0.wireOp",EDGE,"E5.left");var subQ13=sQuery(id+"F0.wireOp",EDGE,"E5.top");var subQ14=sQuery(id+"F0.wireOp",EDGE,"E5.bottom");var subQ15=sQuery(id+"F0.wireOp",EDGE,"E2.right");var subQ16=sQuery(id+"F0.wireOp",EDGE,"E2.left");var subQ17=sQuery(id+"F0.wireOp",EDGE,"E2.top");var subQ18=sQuery(id+"F0.wireOp",EDGE,"E2.bottom");var subQ19=sQuery(id+"F0.wireOp",EDGE,"E1.right");var subQ20=sQuery(id+"F0.wireOp",EDGE,"E1.left");var subQ21=sQuery(id+"F0.wireOp",EDGE,"E1.top");var subQ22=sQuery(id+"F0.wireOp",EDGE,"E1.bottom");var subQ23=makeQuery(id+"F2.opExtrude","CAP_FACE",FACE,{"disambiguationData":[OSD([subQ22,subQ21,subQ20,subQ19,subQ18,subQ17,subQ16,subQ15,subQ14,subQ13,subQ12,subQ11,subQ10,subQ9,subQ8,subQ7,subQ6,subQ5,subQ4,subQ3,subQ2,subQ1,subQ0])],"isStart":false});Q7=makeQuery(id+"F21.opExtrude","CAP_EDGE",EDGE,{"disambiguationData":[OSD([subQ22,subQ21,subQ20,subQ19,subQ18,subQ17,subQ16,subQ15,subQ14,subQ13,subQ12,subQ11,subQ10,subQ9,subQ8,subQ7,subQ6,subQ5,subQ4,subQ3,subQ2,subQ1,subQ0]),TDD([makeQuery(id+"F20.imprint","IMPRINT",EDGE,{"derivedFrom":makeQuery(id+"F17.opChamfer","BLEND_EDGE",EDGE,{"blendedFrom":[makeQuery(id+"F7.opFillet","BLEND_EDGE",EDGE,{"blendedFrom":[makeQuery(id+"F2.opExtrude","SWEPT_EDGE",EDGE,{"disambiguationData":[OSD([subQ21,subQ20])]}),subQ23],"blendedInto":[subQ23]}),subQ23],"blendedInto":[subQ23]})})])],"isStart":false});}
            chamfer(context, id + "F22", {"entities" : qUnion([Q0, Q1, Q2, Q3, Q4, Q5, Q6, Q7]), "width" : 0.2 * mm, "tangentPropagation" : true});
        }
    });
